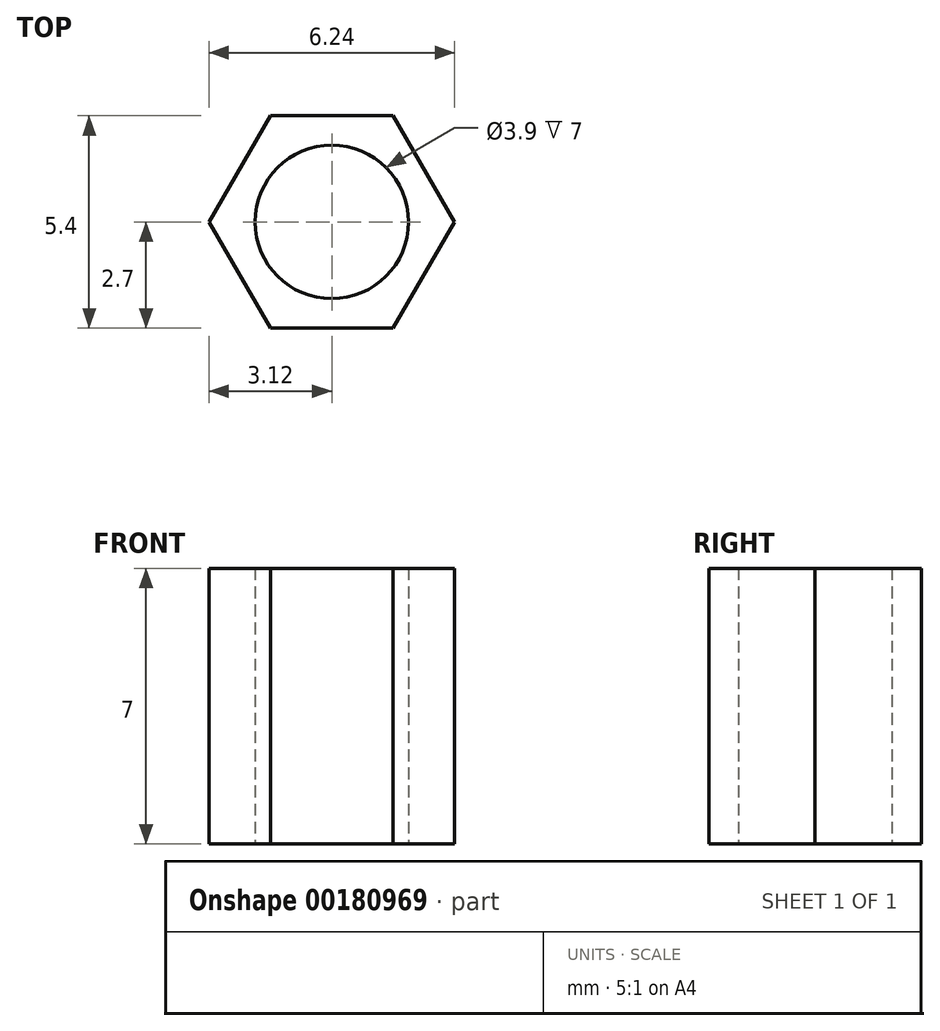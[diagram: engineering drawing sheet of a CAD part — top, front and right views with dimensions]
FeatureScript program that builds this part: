
annotation { "Feature Type Name" : "Feature", "Feature Type Description" : "" }
export const myFeature = defineFeature(function(context is Context, id is Id, definition is map)
    precondition{}
    {
        {
            var Q0;
            Q0=qCreatedBy(makeId("Top.planeOp"),FACE);
            var sketch = newSketch(context, id + "F0", { "sketchPlane" : qUnion([Q0])});
            skCircle(sketch, "E0.cCircle", {"center": v(0, 0) * mm, "radius": 2.7 * mm, "construction": true});
            skLineSegment(sketch, "E0.0", {"start": v(-1.56, 2.7) * mm, "end": v(1.56, 2.7) * mm});
            skLineSegment(sketch, "E0.1", {"start": v(1.56, 2.7) * mm, "end": v(3.12, 0) * mm});
            skLineSegment(sketch, "E0.2", {"start": v(3.12, 0) * mm, "end": v(1.56, -2.7) * mm});
            skLineSegment(sketch, "E0.3", {"start": v(1.56, -2.7) * mm, "end": v(-1.56, -2.7) * mm});
            skLineSegment(sketch, "E0.4", {"start": v(-1.56, -2.7) * mm, "end": v(-3.12, 0) * mm});
            skLineSegment(sketch, "E0.5", {"start": v(-3.12, 0) * mm, "end": v(-1.56, 2.7) * mm});
            skPoint(sketch, "E0.0.midPoint", {"position": v(0, 2.7) * mm});
            skCircle(sketch, "E1", {"center": v(0, 0) * mm, "radius": 1.95 * mm});
            skSolve(sketch);
        }
        {
            var Q0;
            Q0=qSketchRegion(id+"F0",true);
            extrude(context, id + "F1", {"entities" : qUnion([Q0]), "offsetDistance" : 25 * mm, "depth" : 7 * mm});
        }
    });
